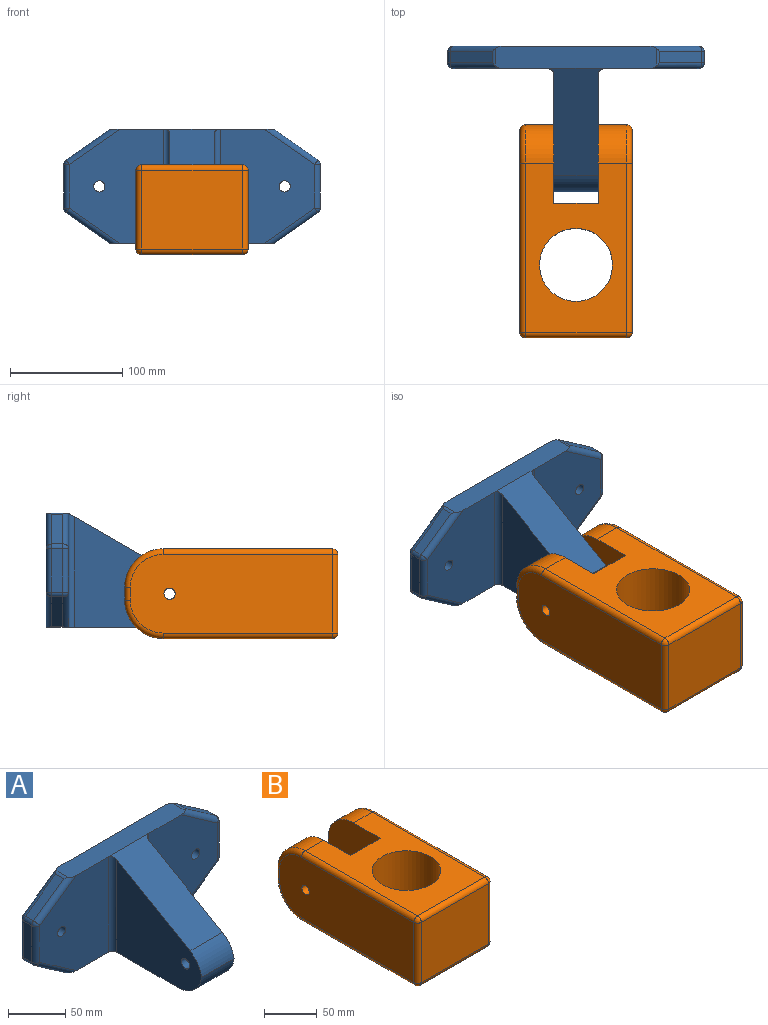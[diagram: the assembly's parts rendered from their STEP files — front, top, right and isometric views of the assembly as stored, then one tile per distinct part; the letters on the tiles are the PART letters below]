
ASSEMBLY  parts=2 mates=1
PART A: 49 faces, bbox 228.6x129.7x109.8 mm
  f0: plane 101.6x84.3mm, normal (0,-1,0), area 7088.8mm2, adj f3,f4,f11,f20,f37,f44,f45
  f1: plane 39.04x10mm, normal (1,0,0), area 390.4mm2, adj f38,f42,f45,f48
  f2: plane 37.53x26.28mm, normal (0.57,0,0.82), area 458.2mm2, adj f35,f36,f37,f38
  f3: plane 143.53x20mm, normal (0,0,1), area 2852.5mm2, adj f0,f5,f6,f13,f21,f22,f24,f35
  f4: cylinder r=5mm len=20mm, axis (0,-1,0), area 628.3mm2, adj f0,f5
  f5: plane 218.6x101.6mm, normal (0,1,0), area 19257.7mm2, adj f3,f4,f9,f11,f24,f29,f34,f36
  f6: plane 101.6x84.3mm, normal (0,-1,0), area 7088.8mm2, adj f3,f9,f11,f19,f21,f26,f31
  f7: plane 39.04x10mm, normal (-1,0,0), area 390.4mm2, adj f25,f26,f29,f30
  f8: plane 37.53x26.28mm, normal (-0.57,0,0.82), area 458.2mm2, adj f21,f22,f24,f25
  f9: cylinder r=5mm len=20mm, axis (0,-1,0), area 628.3mm2, adj f5,f6
  f10: plane 37.53x26.28mm, normal (0.57,0,-0.82), area 458.2mm2, adj f40,f43,f44,f48
  f11: plane 143.53x101.03mm, normal (0,0,-1), area 6104.4mm2, adj f0,f5,f6,f15,f16,f17,f19,f20
  f12: plane 37.53x26.28mm, normal (-0.57,0,-0.82), area 458.2mm2, adj f30,f31,f33,f34
  f13: plane 95.51x55.15mm, normal (0,-0.5,0.87), area 4424mm2, adj f3,f15,f16,f18,f19,f20
  f14: cylinder r=5mm len=40mm, axis (-1,0,0), area 1256.6mm2, adj f15,f16
  f15: plane 104.75x98.71mm, normal (1,0,0), area 6879.1mm2, adj f11,f13,f14,f17,f18,f20
  f16: plane 104.75x98.71mm, normal (-1,0,0), area 6879.1mm2, adj f11,f13,f14,f17,f18,f19
  f17: cylinder r=28.97mm len=40mm, axis (1,0,0), area 1667.7mm2, adj f11,f15,f16,f18
  f18: cylinder r=28.97mm len=40mm, axis (-1,0,0), area 1061mm2, adj f13,f15,f16,f17
  f19: cylinder r=5mm len=101.6mm, axis (0,0,-1), area 789.7mm2, adj f6,f11,f13,f16
  f20: cylinder r=5mm len=101.6mm, axis (0,0,1), area 789.7mm2, adj f0,f11,f13,f15
  f21: cylinder r=5mm len=47.54mm, axis (0.82,0,0.57), area 391mm2, adj f3,f6,f8,f22,f23
  f22: cylinder r=5mm len=15.74mm, axis (0,-1,0), area 39.6mm2, adj f3,f8,f21,f24
  f23: sphere r=5mm, area 24mm2, adj f21,f25,f26
  f24: cylinder r=5mm len=47.54mm, axis (-0.82,0,-0.57), area 391mm2, adj f3,f5,f8,f22,f27
  f25: cylinder r=5mm len=10mm, axis (0,-1,0), area 48mm2, adj f7,f8,f23,f27
  f26: cylinder r=5mm len=39.04mm, axis (0,0,1), area 306.6mm2, adj f6,f7,f23,f28
  f27: sphere r=5mm, area 24mm2, adj f24,f25,f29
  f28: sphere r=5mm, area 24mm2, adj f26,f30,f31
  f29: cylinder r=5mm len=39.04mm, axis (0,0,-1), area 306.6mm2, adj f5,f7,f27,f32
  f30: cylinder r=5mm len=10mm, axis (0,-1,0), area 48mm2, adj f7,f12,f28,f32
  f31: cylinder r=5mm len=47.54mm, axis (0.82,0,-0.57), area 391mm2, adj f6,f11,f12,f28,f33
  f32: sphere r=5mm, area 24mm2, adj f29,f30,f34
  f33: cylinder r=5mm len=15.74mm, axis (0,-1,0), area 39.6mm2, adj f11,f12,f31,f34
  f34: cylinder r=5mm len=47.54mm, axis (-0.82,0,0.57), area 391mm2, adj f5,f11,f12,f32,f33
  f35: cylinder r=5mm len=15.74mm, axis (0,-1,0), area 39.6mm2, adj f2,f3,f36,f37
  f36: cylinder r=5mm len=47.54mm, axis (0.82,0,-0.57), area 391mm2, adj f2,f3,f5,f35,f39
  f37: cylinder r=5mm len=47.54mm, axis (-0.82,0,0.57), area 391mm2, adj f0,f2,f3,f35,f41
  f38: cylinder r=5mm len=10mm, axis (0,-1,0), area 48mm2, adj f1,f2,f39,f41
  f39: sphere r=5mm, area 24mm2, adj f36,f38,f42
  f40: cylinder r=5mm len=15.74mm, axis (0,-1,0), area 39.6mm2, adj f10,f11,f43,f44
  f41: sphere r=5mm, area 24mm2, adj f37,f38,f45
  f42: cylinder r=5mm len=39.04mm, axis (0,0,-1), area 306.6mm2, adj f1,f5,f39,f46
  f43: cylinder r=5mm len=47.54mm, axis (0.82,0,0.57), area 391mm2, adj f5,f10,f11,f40,f46
  f44: cylinder r=5mm len=47.54mm, axis (-0.82,0,-0.57), area 391mm2, adj f0,f10,f11,f40,f47
  f45: cylinder r=5mm len=39.04mm, axis (0,0,1), area 306.6mm2, adj f0,f1,f41,f47
  f46: sphere r=5mm, area 24mm2, adj f42,f43,f48
  f47: sphere r=5mm, area 24mm2, adj f44,f45,f48
  f48: cylinder r=5mm len=10mm, axis (0,-1,0), area 48mm2, adj f1,f10,f46,f47
PART B: 35 faces, bbox 100x192.8x85.6 mm
  f0: plane 25x11.44mm, normal (0,1,0), area 285.9mm2, adj f1,f12,f14,f31
  f1: plane 80x70mm, normal (-1,0,0), area 5017mm2, adj f0,f2,f9,f10,f12,f14,f33
  f2: plane 80x40mm, normal (0,1,0), area 3200mm2, adj f1,f3,f9,f10
  f3: plane 80x70mm, normal (1,0,0), area 5017mm2, adj f2,f4,f9,f10,f11,f13,f34
  f4: plane 25x11.44mm, normal (0,1,0), area 285.9mm2, adj f3,f11,f13,f16
  f5: plane 180x70mm, normal (-1,0,0), area 12153.4mm2, adj f15,f16,f17,f18,f20,f21,f34
  f6: plane 90x70mm, normal (0,-1,0), area 6300mm2, adj f21,f22,f25,f26
  f7: plane 180x70mm, normal (1,0,0), area 12153.4mm2, adj f26,f27,f29,f30,f31,f32,f33
  f8: cylinder r=32.5mm len=80mm, axis (0,0,-1), area 16336.3mm2, adj f9,f10
  f9: plane 150.72x90mm, normal (0,0,1), area 8817.6mm2, adj f1,f2,f3,f8,f13,f14,f17,f22
  f10: plane 150.72x90mm, normal (0,0,-1), area 8817.6mm2, adj f1,f2,f3,f8,f11,f12,f20,f25
  f11: cylinder r=34.28mm len=34.28mm, axis (-1,0,0), area 1346.2mm2, adj f3,f4,f10,f18
  f12: cylinder r=34.28mm len=34.28mm, axis (-1,0,0), area 1346.2mm2, adj f0,f1,f10,f32
  f13: cylinder r=34.28mm len=34.28mm, axis (1,0,0), area 1346.2mm2, adj f3,f4,f9,f15
  f14: cylinder r=34.28mm len=34.28mm, axis (1,0,0), area 1346.2mm2, adj f0,f1,f9,f29
  f15: torus R=29.28mm, axis (-1,0,0), area 400.5mm2, adj f5,f13,f16,f17
  f16: cylinder r=5mm len=11.44mm, axis (0,0,-1), area 89.8mm2, adj f4,f5,f15,f18
  f17: cylinder r=5mm len=150.72mm, axis (0,1,0), area 1183.7mm2, adj f5,f9,f15,f19
  f18: torus R=29.28mm, axis (-1,0,0), area 400.5mm2, adj f5,f11,f16,f20
  f19: sphere r=5mm, area 39.3mm2, adj f17,f21,f22
  f20: cylinder r=5mm len=150.72mm, axis (0,-1,0), area 1183.7mm2, adj f5,f10,f18,f23
  f21: cylinder r=5mm len=70mm, axis (0,0,-1), area 549.8mm2, adj f5,f6,f19,f23
  f22: cylinder r=5mm len=90mm, axis (-1,0,0), area 706.9mm2, adj f6,f9,f19,f24
  f23: sphere r=5mm, area 39.3mm2, adj f20,f21,f25
  f24: sphere r=5mm, area 39.3mm2, adj f22,f26,f27
  f25: cylinder r=5mm len=90mm, axis (1,0,0), area 706.9mm2, adj f6,f10,f23,f28
  f26: cylinder r=5mm len=70mm, axis (0,0,-1), area 549.8mm2, adj f6,f7,f24,f28
  f27: cylinder r=5mm len=150.72mm, axis (0,-1,0), area 1183.7mm2, adj f7,f9,f24,f29
  f28: sphere r=5mm, area 39.3mm2, adj f25,f26,f30
  f29: torus R=29.28mm, axis (1,0,0), area 400.5mm2, adj f7,f14,f27,f31
  f30: cylinder r=5mm len=150.72mm, axis (0,1,0), area 1183.7mm2, adj f7,f10,f28,f32
  f31: cylinder r=5mm len=11.44mm, axis (0,0,-1), area 89.8mm2, adj f0,f7,f29,f32
  f32: torus R=29.28mm, axis (1,0,0), area 400.5mm2, adj f7,f12,f30,f31
  f33: cylinder r=5mm len=30mm, axis (-1,0,0), area 942.5mm2, adj f1,f7
  f34: cylinder r=5mm len=30mm, axis (-1,0,0), area 942.5mm2, adj f3,f5
PLACE A t=(-64,425.6,105.39)mm
PLACE B t=(-114,185.6,44.59)mm
MATE revolute A.f14 <-> B.f33  axis (1,0,0) through (-44,335.6,84.59)mm
